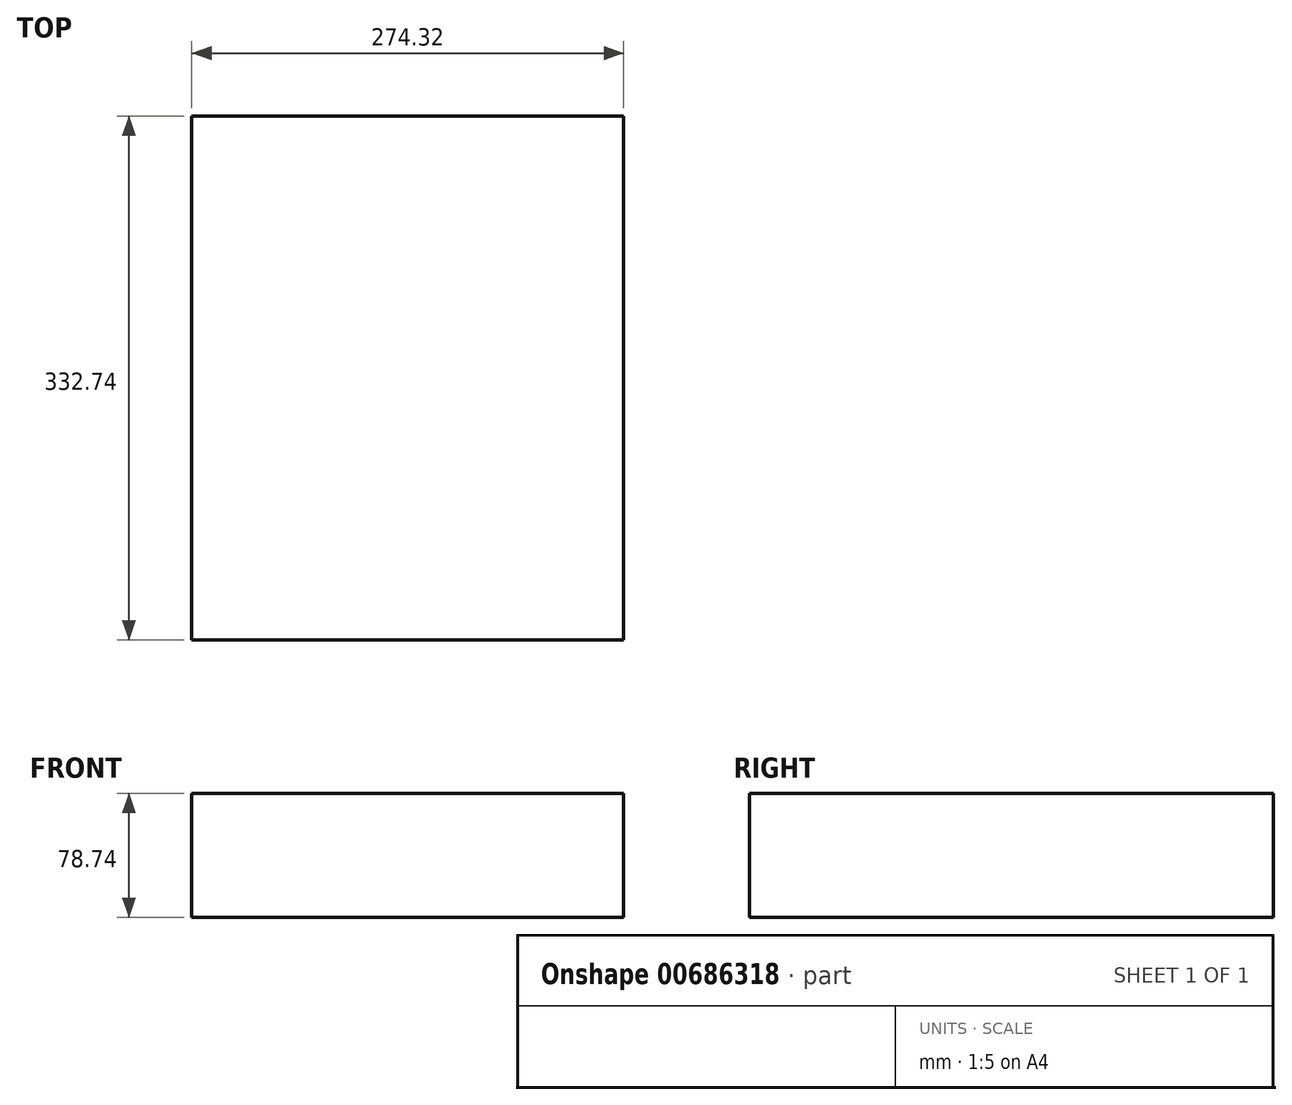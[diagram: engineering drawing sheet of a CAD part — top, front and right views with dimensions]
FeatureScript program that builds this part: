
annotation { "Feature Type Name" : "Feature", "Feature Type Description" : "" }
export const myFeature = defineFeature(function(context is Context, id is Id, definition is map)
    precondition{}
    {
        {
            var Q0;
            Q0=qCreatedBy(makeId("Right.planeOp"),FACE);
            var sketch = newSketch(context, id + "F0", { "sketchPlane" : qUnion([Q0])});
            skLineSegment(sketch, "E0.bottom", {"start": v(166.37, 39.37) * mm, "end": v(-166.37, 39.37) * mm});
            skLineSegment(sketch, "E0.top", {"start": v(166.37, -39.37) * mm, "end": v(-166.37, -39.37) * mm});
            skLineSegment(sketch, "E0.left", {"start": v(166.37, 39.37) * mm, "end": v(166.37, -39.37) * mm});
            skLineSegment(sketch, "E0.right", {"start": v(-166.37, 39.37) * mm, "end": v(-166.37, -39.37) * mm});
            skPoint(sketch, "E0.middle", {"position": v(0, 0) * mm});
            skSolve(sketch);
        }
        {
            var Q0;
            Q0 = qSketchRegion(id + "F0", true);
            extrude(context, id + "F1", {"entities" : qUnion([Q0]), "endBound" : BoundingType.SYMMETRIC, "depth" : 274.32 * mm, "offsetDistance" : 25.4 * mm});
        }
    });
